# Revit family: 0047040 START PANEL FLAT UGR19 600X600 840 SSH
name_source: partatom
category: Lighting Fixtures
revit_build: Autodesk Revit 2016 (Build: 20150220_1215(x64)
units: mm (PartAtom-declared; Revit-internal decimal feet)

## family parameters
Cut with Voids When Loaded = No
Host = Face
Light Source = Yes
OmniClass Number = 23.80.70.00
OmniClass Title = Lighting
Part Type = Normal
Room Calculation Point = No
Round Connector Dimension = Use Diameter
Shared = No

## types (1)
- 0047040 START PANEL FLAT UGR19 600X600 840 SSH
    Apparent Load = 32 VA
    Assembly Code = D5020200
    AssetType = Fixed
    ClassificationName = Uniclass2015
    ClassificationValue = EF_70_80
    Color Filter = 16777215
    Cost = 0 $
    Default Elevation = 1219 mm
    Dimming Lamp Color Temperature Shift = <None>
    DocumentationLiterature = http://www.sylvania-lighting.com
    DurationUnit = hours
    ElectricShockClassification = Class II
    Emit Shape Visible in Rendering = No
    Emit from Rectangle Length = 540 mm
    Emit from Rectangle Width = 540 mm
    ExpectedLife = 50000
    IfcExportAs = IfcLightFixtureType
    IfcExportType = IfcLightFixtureType
    ImpactProtectionIndex = IK06
    IngressProtection = IP20/40
    InputNominalFrequency = 50/60 Hz
    InputVoltage = 220-240V~
    Keynote = 16500
    Lamp = LED
    LampColourRenderingIndex = 80
    LampColourTemperature = 4000 K
    LampNominalLuminous = 3500 lm
    LampsType = LED
    LengthInner_SYL = 530 mm  [stored 1.73885 ft]
    Length_SYL = 596 mm  [stored 1.95538 ft]
    LuminousEfficacy = 109.3 lm/W
    Manufacturer = Feilo Sylvania
    ManufacturerName = Feilo Sylvania
    Material_1_FEILO = Body-Sylvania-StartFlat-White
    Material_2_FEILO = LED-Sylvania-StartFlat
    Material_3_FEILO = <By Category>
    Material_4_FEILO = <By Category>
    Model = START PANEL FLAT UGR19 600X600 840 SSH
    ModelNumber = 0047040
    ModelReference = START PANEL FLAT UGR19 600X600 840 SSH
    Name = START PANEL FLAT UGR19 600X600 840 SSH
    NominalDepth = 596 mm  [stored 1.95538 ft]
    NominalHeight = 50 mm
    NominalLength = 596 mm  [stored 1.95538 ft]
    Photometric Web File = 0047040.ies
    PowerConsumption = 32 W
    PowerFactor = 0
    Tilt Angle = -90.00°
    Type Image = <None>
    TypeName = START PANEL FLAT UGR19 600X600 840 SSH
    URL = http://www.sylvania-lighting.com
    Voltage = 230 V
    Weight = 4.4 kg

note: [stored X ft] marks values corroborated as IEEE doubles in the binary element streams (Revit-internal decimal feet)

## geometry (parser evidence)
native form markers: Sweep x3
no freeform markers — native parametric forms only
